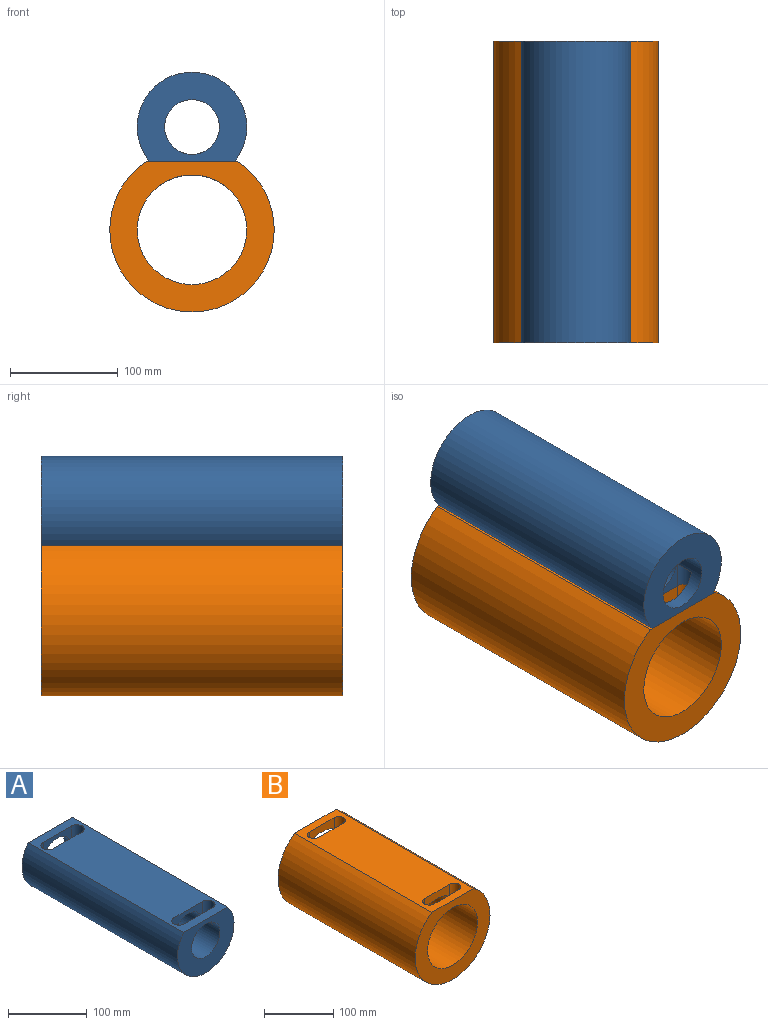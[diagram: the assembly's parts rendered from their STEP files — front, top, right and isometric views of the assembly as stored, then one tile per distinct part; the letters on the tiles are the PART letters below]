
ASSEMBLY  parts=2 mates=1
PART A: 17 faces, bbox 101.6x279.4x82.6 mm
  f0: cylinder r=25.4mm len=279.4mm, axis (0,1,0), area 42039.1mm2, adj f3,f4,f5,f7,f9,f10,f11,f12
  f1: plane 279.4x79.31mm, normal (0,0,1), area 19654.1mm2, adj f2,f3,f4,f6,f7,f8,f9,f12
  f2: cylinder r=50.8mm len=279.4mm, axis (0,1,0), area 63755.2mm2, adj f1,f3,f4
  f3: plane 101.6x82.55mm, normal (0,-1,0), area 5028.2mm2, adj f0,f1,f2
  f4: plane 101.6x82.55mm, normal (0,1,0), area 5028.2mm2, adj f0,f1,f2
  f5: plane 19.05x10.33mm, normal (0,0,1), area 157.9mm2, adj f0,f7,f8,f9
  f6: cylinder r=9.53mm len=25.4mm, axis (0,0,1), area 760.1mm2, adj f1,f7,f9,f10
  f7: plane 50.8x25.4mm, normal (0,1,0), area 596.1mm2, adj f0,f1,f5,f6,f8,f10
  f8: cylinder r=9.53mm len=25.4mm, axis (0,0,1), area 760.1mm2, adj f1,f5,f7,f9
  f9: plane 50.8x25.4mm, normal (0,-1,0), area 596.1mm2, adj f0,f1,f5,f6,f8,f10
  f10: plane 19.05x10.33mm, normal (0,0,1), area 157.9mm2, adj f0,f6,f7,f9
  f11: plane 19.05x10.33mm, normal (0,0,1), area 157.9mm2, adj f0,f12,f13,f14
  f12: plane 50.8x25.4mm, normal (0,1,0), area 596.1mm2, adj f0,f1,f11,f13,f15,f16
  f13: cylinder r=9.53mm len=25.4mm, axis (0,0,1), area 760.1mm2, adj f1,f11,f12,f14
  f14: plane 50.8x25.4mm, normal (0,-1,0), area 596.1mm2, adj f0,f1,f11,f13,f15,f16
  f15: cylinder r=9.53mm len=25.4mm, axis (0,0,1), area 760.1mm2, adj f1,f12,f14,f16
  f16: plane 19.05x10.33mm, normal (0,0,1), area 157.9mm2, adj f0,f12,f14,f15
PART B: 13 faces, bbox 152.4x279.4x139.7 mm
  f0: cylinder r=50.8mm len=279.4mm, axis (0,1,0), area 86450.2mm2, adj f3,f4,f5,f6,f7,f8,f9,f10
  f1: plane 279.4x84.24mm, normal (0,0,1), area 21031.8mm2, adj f2,f3,f4,f5,f6,f7,f8,f9
  f2: cylinder r=76.2mm len=279.4mm, axis (0,1,0), area 108832mm2, adj f1,f3,f4
  f3: plane 152.4x139.7mm, normal (0,-1,0), area 9408.1mm2, adj f0,f1,f2
  f4: plane 152.4x139.7mm, normal (0,1,0), area 9408.1mm2, adj f0,f1,f2
  f5: plane 50.8x19.51mm, normal (0,1,0), area 757.1mm2, adj f0,f1,f6,f7
  f6: cylinder r=9.53mm len=26.61mm, axis (0,0,1), area 711.8mm2, adj f0,f1,f5,f8
  f7: cylinder r=9.53mm len=26.61mm, axis (0,0,1), area 711.8mm2, adj f0,f1,f5,f8
  f8: plane 50.8x19.51mm, normal (0,-1,0), area 757.1mm2, adj f0,f1,f6,f7
  f9: cylinder r=9.53mm len=26.61mm, axis (0,0,1), area 711.8mm2, adj f0,f1,f10,f11
  f10: plane 50.8x19.51mm, normal (0,1,0), area 757.1mm2, adj f0,f1,f9,f12
  f11: plane 50.8x19.51mm, normal (0,-1,0), area 757.1mm2, adj f0,f1,f9,f12
  f12: cylinder r=9.53mm len=26.61mm, axis (0,0,1), area 711.8mm2, adj f0,f1,f10,f11
PLACE A rot(axis=(0,1,0),180deg) t=(9.07,0,174.19)mm
PLACE B t=(9.07,0,78.94)mm
MATE planar B.f1 <-> A.f1  axis (0,0,1) through (9.07,0,142.44)mm
